# Revit family: LAMP_KOMBIC 150 SURFACE TW OPTIC
name_source: partatom
category: Luminarias
revit_build: Autodesk Revit 2018 (Build: 20190510_1515(x64)
units: mm (PartAtom-declared; Revit-internal decimal feet)

## family parameters
Anfitrión = Cara
Compartido = No
Corte con vacíos al cargar = No
Cota de conector redondo = Diámetro de uso
Origen de luz = Sí
Punto de cálculo de habitación = No
Tipo de pieza = Normal

## types (6) — shared parameters
CRI = 90
Cambio de temperatura de color de luz atenuada = <Ninguno>
Diameter = 150 mm
Elevación por defecto = 1219 mm
Fabricante = LAMP
Filtro de color = 16777215
Gear = Electronic
Height = 180 mm  [stored 0.590551 ft]
IEE = A
Initial color = 2700-5000
Installation instructions = https://www.lamp.es
Insulation class = II
LED Lifetime = 50.000 L80 B10
Lamp = COB LED
Last update = 14/10/2021
Luminaire type = Suspended
MacAdam = 3
Manufacturer URL = http://www.lamp.es
Manufacturer country = Spain
Manufacturer name = LAMP
Material cable suspension = LAMP_Acero genérico
Material difusor = LAMP_PMMA Difusor Kombic
Model explanation = Possibility of chossing between surface or suspended within the model
Plum = 24 W
Power = 20 W
Power Supply = 220-240V 50/60Hz
Product URL = https://www.lamp.es
Product datasheet = http://www.lamp.es
Protection rating = IP40
Type = COB BRIDGELUX
UGR = 19
Ángulo de inclinación = -90.00°

## per-type parameters (varying)
| type | Archivo de red fotométrica | Efficacy | Finish | Material cuerpo | Material floron | Material reflector | Modelo | Product code | Weight |
| 1413LM 2700-5000K DALI B/B | K21SF3040WF9TWDBB.IES | 60 lm/W | Matte black RAL 9011 | LAMP_Plástico genérico NG | LAMP_Plástico genérico NG | LAMP_PC Reflector Kombic Metalizado Negro | K21SF3040WF9TWDBB | K21SF3040WF9TWDBB | 1.74 kg |
| 1413LM 2700-5000K DALI B/W | K21SF3040WF9TWDBW.IES | 59 lm/W | Matte white RAL 9010 | LAMP_Plástico genérico BL | LAMP_Plástico genérico BL | LAMP_PC Reflector Kombic Metalizado Negro | K21SF3040WF9TWDBW | K21SF3040WF9TWDBW | 1.74 kg |
| 1423LM 2700-5000K DALI M/B | K21SF3040WF9TWDMB.IES | 60 lm/W | Matte white RAL 9010 | LAMP_Plástico genérico NG | LAMP_Plástico genérico NG | LAMP_PC Reflector Kombic Metalizado Mate | K21SF3040WF9TWDMB | K21SF3040WF9TWDMB | 1.59 kg |
| 1423LM 2700-5000K DALI M/W | K21SF3040WF9TWDMW.IES | 60 lm/W | Matte black RAL 9011 | LAMP_Plástico genérico BL | LAMP_Plástico genérico BL | LAMP_PC Reflector Kombic Metalizado Mate | K21SF3040WF9TWDMW | K21SF3040WF9TWDMW | 1.59 kg |
| 1443LM 2700-5000K DALI W/B | K21SF3040WF9TWDWB.IES | 61 lm/W | Matte white RAL 9010 | LAMP_Plástico genérico NG | LAMP_Plástico genérico NG | LAMP_PC Reflector Kombic Blanco | K21SF3040WF9TWDWB | K21SF3040WF9TWDWB | 1.59 kg |
| 1443LM 2700-5000K DALI W/W | K21SF3040WF9TWDWW.IES | 61 lm/W | Matte black RAL 9011 | LAMP_Plástico genérico BL | LAMP_Plástico genérico BL | LAMP_PC Reflector Kombic Blanco | K21SF3040WF9TWDWW | K21SF3040WF9TWDWW | 1.59 kg |

note: [stored X ft] marks values corroborated as IEEE doubles in the binary element streams (Revit-internal decimal feet)
